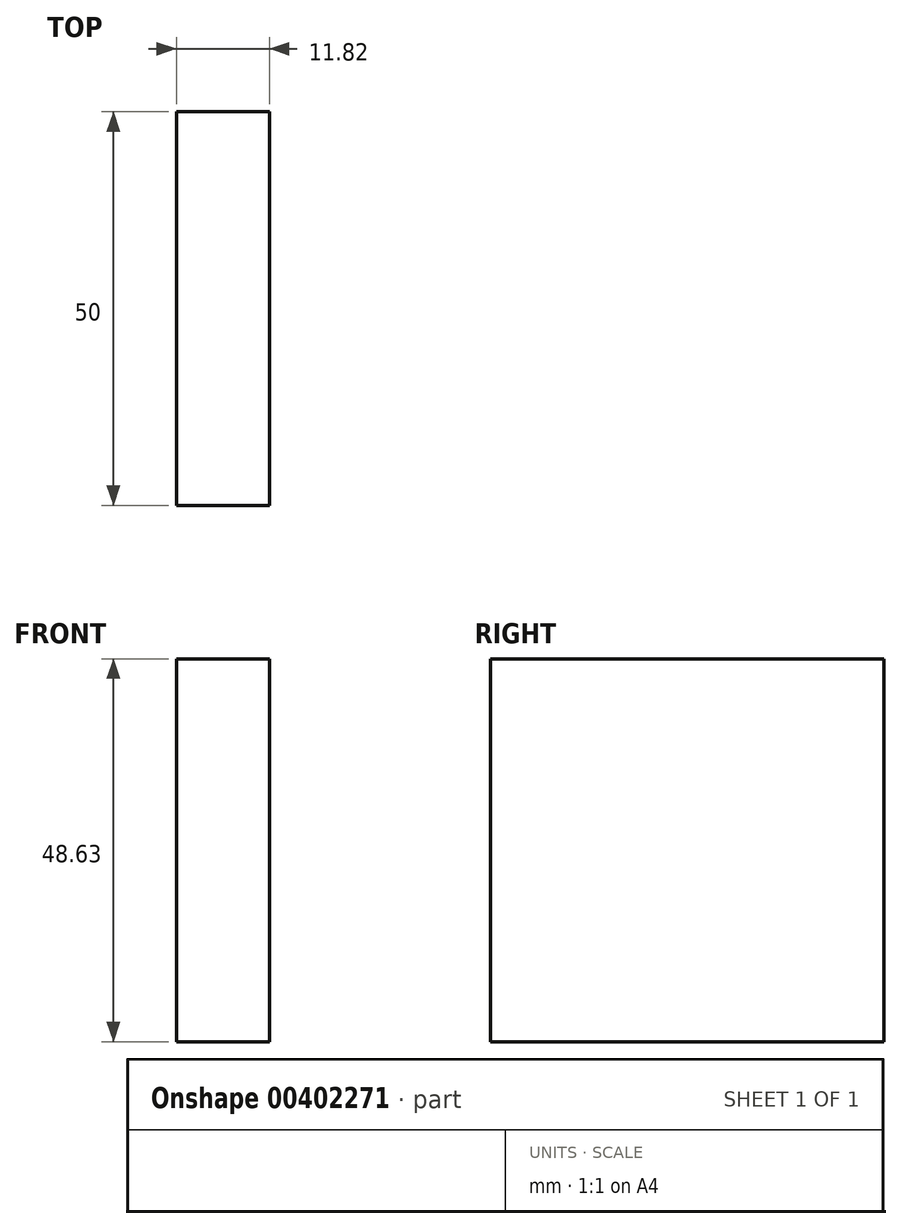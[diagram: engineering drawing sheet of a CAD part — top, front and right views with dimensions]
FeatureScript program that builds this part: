
annotation { "Feature Type Name" : "Feature", "Feature Type Description" : "" }
export const myFeature = defineFeature(function(context is Context, id is Id, definition is map)
    precondition{}
    {
        {
            var Q0;
            Q0=qCreatedBy(makeId("Front.planeOp"),FACE);
            var sketch = newSketch(context, id + "F0", { "sketchPlane" : qUnion([Q0])});
            skLineSegment(sketch, "E0.bottom", {"start": v(0, 0) * mm, "end": v(0, 0) * mm});
            skLineSegment(sketch, "E0.top", {"start": v(0, 0) * mm, "end": v(0, 0) * mm});
            skLineSegment(sketch, "E0.left", {"start": v(0, 0) * mm, "end": v(0, 0) * mm});
            skLineSegment(sketch, "E0.right", {"start": v(0, 0) * mm, "end": v(0, 0) * mm});
            skLineSegment(sketch, "E1.bottom", {"start": v(26.69, 22.19) * mm, "end": v(14.87, 22.19) * mm});
            skLineSegment(sketch, "E1.top", {"start": v(26.69, -26.44) * mm, "end": v(14.87, -26.44) * mm});
            skLineSegment(sketch, "E1.left", {"start": v(26.69, -26.44) * mm, "end": v(26.69, 22.19) * mm});
            skLineSegment(sketch, "E1.right", {"start": v(14.87, -26.44) * mm, "end": v(14.87, 22.19) * mm});
            skPoint(sketch, "E1.middle", {"position": v(20.78, -2.13) * mm});
            skSolve(sketch);
        }
        {
            var Q0;
            Q0=makeQuery(id+"F0.imprint","IMPRINT",FACE,{"disambiguationData":[TD([[makeQuery(id+"F0.imprint","IMPRINT",EDGE,{"derivedFrom":sQuery(id+"F0.wireOp",EDGE,"E1.bottom")}),1.0]])]});
            extrude(context, id + "F1", {"entities" : qUnion([Q0]), "endBound" : BoundingType.SYMMETRIC, "depth" : 50 * mm});
        }
    });
